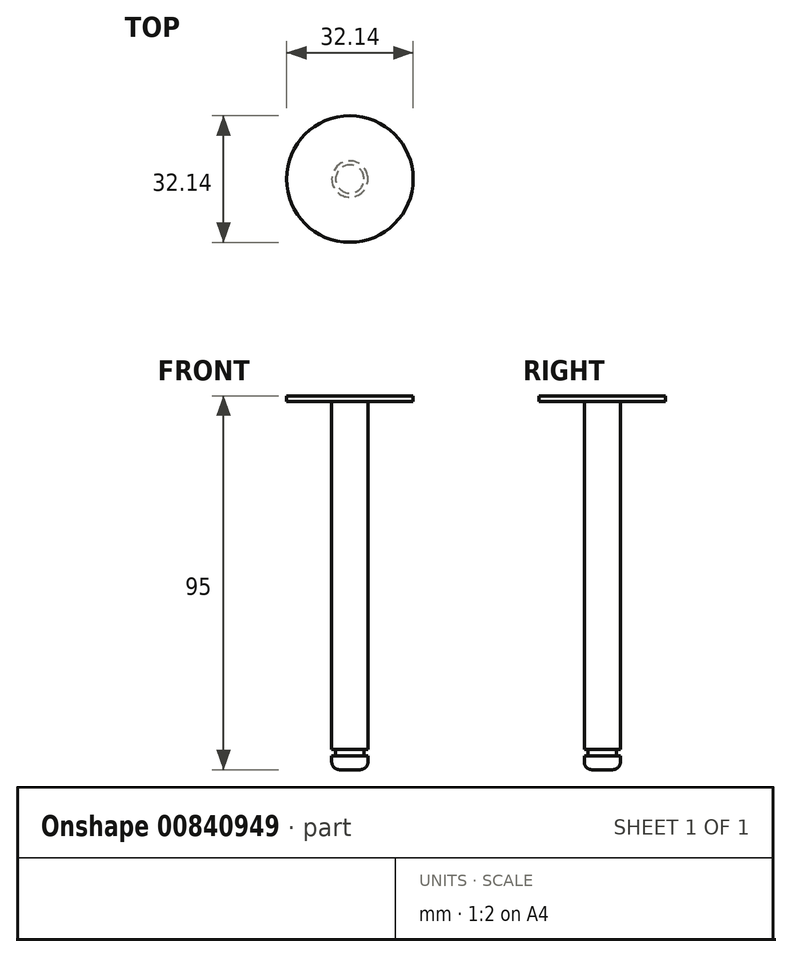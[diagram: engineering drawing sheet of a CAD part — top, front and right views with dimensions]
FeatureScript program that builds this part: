
annotation { "Feature Type Name" : "Feature", "Feature Type Description" : "" }
export const myFeature = defineFeature(function(context is Context, id is Id, definition is map)
    precondition{}
    {
        {
            var Q0;
            Q0=qCreatedBy(makeId("Front.planeOp"),FACE);
            var sketch = newSketch(context, id + "F0", { "sketchPlane" : qUnion([Q0])});
            skLineSegment(sketch, "E0", {"start": v(0, 0) * mm, "end": v(-4.6, 0) * mm});
            skLineSegment(sketch, "E1", {"start": v(-4.6, 0) * mm, "end": v(-4.6, 3.5) * mm});
            skLineSegment(sketch, "E2", {"start": v(-4.6, 3.5) * mm, "end": v(-3.6, 3.5) * mm});
            skLineSegment(sketch, "E3", {"start": v(-3.6, 3.5) * mm, "end": v(-3.6, 5.2) * mm});
            skLineSegment(sketch, "E4", {"start": v(-3.6, 5.2) * mm, "end": v(-4.6, 5.2) * mm});
            skLineSegment(sketch, "E5", {"start": v(-4.6, 5.2) * mm, "end": v(-4.6, 93.5) * mm});
            skLineSegment(sketch, "E6", {"start": v(-4.6, 93.5) * mm, "end": v(-16.07, 93.5) * mm});
            skLineSegment(sketch, "E7", {"start": v(-16.07, 93.5) * mm, "end": v(-16.07, 95) * mm});
            skLineSegment(sketch, "E8", {"start": v(-16.07, 95) * mm, "end": v(0, 95) * mm});
            skLineSegment(sketch, "E9", {"start": v(0, 95) * mm, "end": v(0, 0) * mm});
            skSolve(sketch);
        }
        {
            var Q0;
            Q0=makeQuery(id+"F0.imprint","IMPRINT",FACE,{"disambiguationData":[TD([[makeQuery(id+"F0.imprint","IMPRINT",EDGE,{"derivedFrom":sQuery(id+"F0.wireOp",EDGE,"E0")}),-1.0]])]});
            var Q1;
            Q1=sQuery(id+"F0.wireOp",EDGE,"E9");
            revolve(context, id + "F1", {"surfaceOperationType" : NewSurfaceOperationType.NEW, "entities" : qUnion([Q0]), "axis" : qUnion([Q1]), "revolveType" : RevolveType.FULL});
        }
        {
            var Q0;
            Q0=makeQuery(id+"F1.opRevolve","SWEPT_EDGE",EDGE,{"disambiguationData":[OSD([sQuery(id+"F0.wireOp",EDGE,"E0"),sQuery(id+"F0.wireOp",EDGE,"E1")])]});
            fillet(context, id + "F2", {"entities" : qUnion([Q0]), "radius" : 2 * mm, "tangentPropagation" : true, "allowEdgeOverflow" : false});
        }
    });
